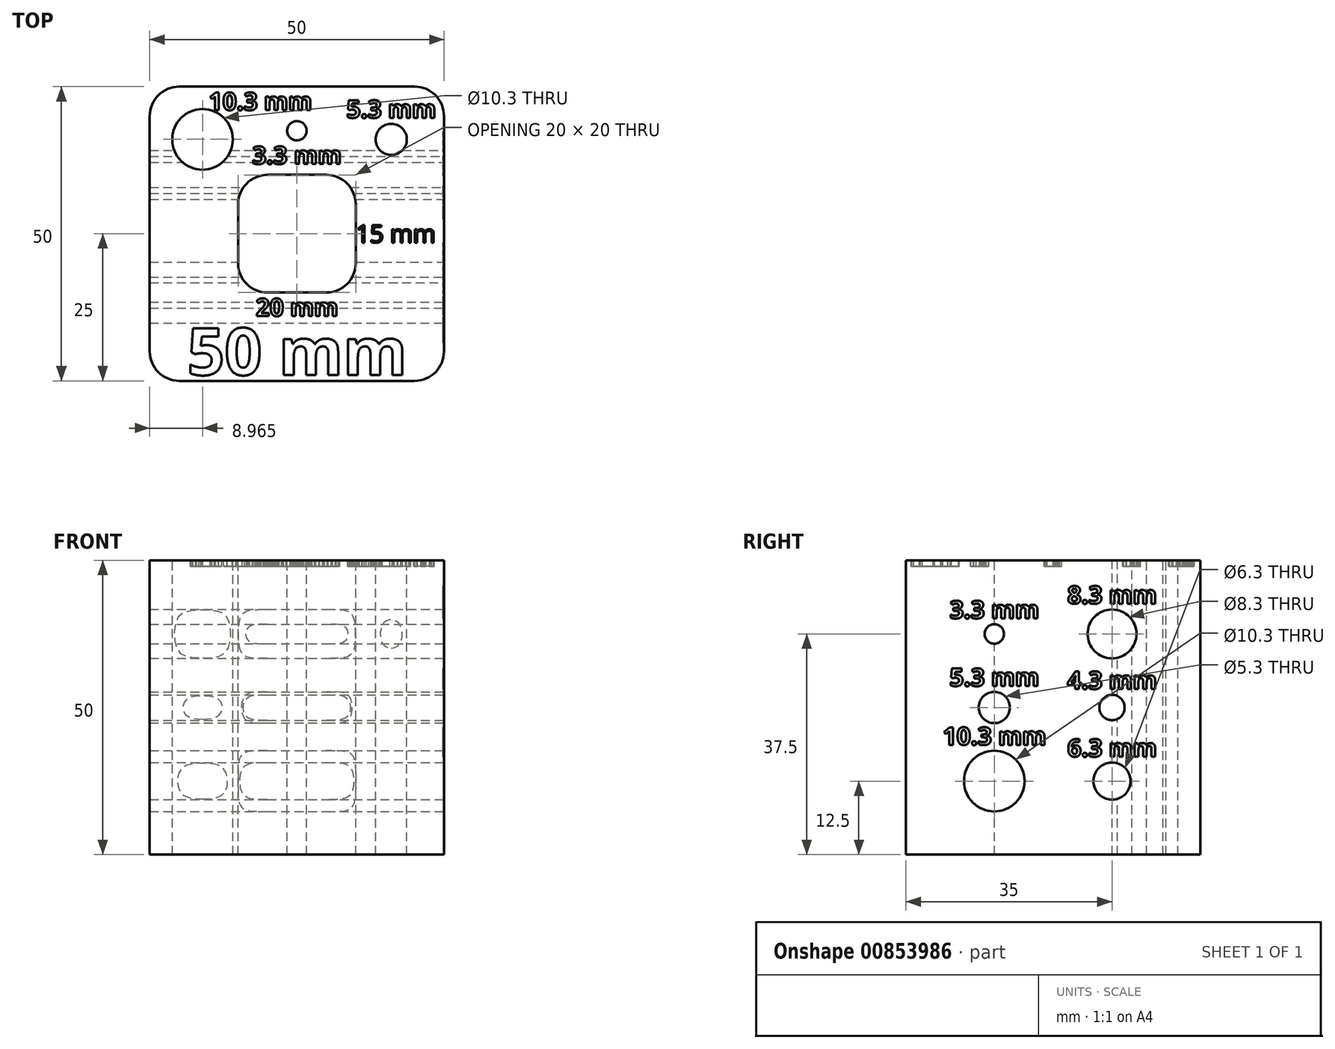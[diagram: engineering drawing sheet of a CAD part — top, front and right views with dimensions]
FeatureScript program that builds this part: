
annotation { "Feature Type Name" : "Feature", "Feature Type Description" : "" }
export const myFeature = defineFeature(function(context is Context, id is Id, definition is map)
    precondition{}
    {
        {
            var Q0;
            Q0=qCreatedBy(makeId("Top.planeOp"),FACE);
            var sketch = newSketch(context, id + "F0", { "sketchPlane" : qUnion([Q0])});
            skLineSegment(sketch, "E0.bottom", {"start": v(-25, 25) * mm, "end": v(25, 25) * mm});
            skLineSegment(sketch, "E0.top", {"start": v(-25, -25) * mm, "end": v(25, -25) * mm});
            skLineSegment(sketch, "E0.left", {"start": v(-25, 25) * mm, "end": v(-25, -25) * mm});
            skLineSegment(sketch, "E0.right", {"start": v(25, 25) * mm, "end": v(25, -25) * mm});
            skLineSegment(sketch, "E1", {"start": v(0, 25) * mm, "end": v(0, -25) * mm, "construction": true});
            skSolve(sketch);
        }
        {
            var Q0;
            Q0=makeQuery(id+"F0.imprint","IMPRINT",FACE,{"disambiguationData":[TD([[makeQuery(id+"F0.imprint","IMPRINT",EDGE,{"derivedFrom":sQuery(id+"F0.wireOp",EDGE,"E0.bottom")}),-1.0]])]});
            extrude(context, id + "F1", {"entities" : qUnion([Q0]), "depth" : 50 * mm, "offsetDistance" : 25 * mm});
        }
        {
            var Q0;
            Q0=makeQuery(id+"F1.opExtrude","CAP_FACE",FACE,{"disambiguationData":[OSD([sQuery(id+"F0.wireOp",EDGE,"E0.bottom"),sQuery(id+"F0.wireOp",EDGE,"E0.top"),sQuery(id+"F0.wireOp",EDGE,"E0.left"),sQuery(id+"F0.wireOp",EDGE,"E0.right")])],"isStart":false});
            var sketch = newSketch(context, id + "F2", { "sketchPlane" : qUnion([Q0])});
            skLineSegment(sketch, "E2.bottom", {"start": v(-10, 10) * mm, "end": v(10, 10) * mm});
            skLineSegment(sketch, "E2.top", {"start": v(-10, -10) * mm, "end": v(10, -10) * mm});
            skLineSegment(sketch, "E2.left", {"start": v(-10, 10) * mm, "end": v(-10, -10) * mm});
            skLineSegment(sketch, "E2.right", {"start": v(10, 10) * mm, "end": v(10, -10) * mm});
            skLineSegment(sketch, "E3", {"start": v(0, 10) * mm, "end": v(0, -10) * mm, "construction": true});
            skSolve(sketch);
        }
        {
            var Q0;
            Q0=makeQuery(id+"F2.imprint","IMPRINT",FACE,{"disambiguationData":[TD([[makeQuery(id+"F2.imprint","IMPRINT",EDGE,{"derivedFrom":sQuery(id+"F2.wireOp",EDGE,"E2.bottom")}),-1.0]])]});
            extrude(context, id + "F3", {"entities" : qUnion([Q0]), "operationType" : NewBodyOperationType.REMOVE, "endBound" : BoundingType.THROUGH_ALL, "oppositeDirection" : true, "depth" : 25 * mm, "offsetDistance" : 25 * mm});
        }
        {
            var Q0;
            Q0=makeQuery(id+"F1.opExtrude","SWEPT_EDGE",EDGE,{"disambiguationData":[OSD([sQuery(id+"F0.wireOp",EDGE,"E0.bottom"),sQuery(id+"F0.wireOp",EDGE,"E0.left")])]});
            var Q1;
            Q1=makeQuery(id+"F1.opExtrude","SWEPT_EDGE",EDGE,{"disambiguationData":[OSD([sQuery(id+"F0.wireOp",EDGE,"E0.bottom"),sQuery(id+"F0.wireOp",EDGE,"E0.right")])]});
            var Q2;
            Q2=makeQuery(id+"F1.opExtrude","SWEPT_EDGE",EDGE,{"disambiguationData":[OSD([sQuery(id+"F0.wireOp",EDGE,"E0.top"),sQuery(id+"F0.wireOp",EDGE,"E0.right")])]});
            var Q3;
            Q3=makeQuery(id+"F1.opExtrude","SWEPT_EDGE",EDGE,{"disambiguationData":[OSD([sQuery(id+"F0.wireOp",EDGE,"E0.top"),sQuery(id+"F0.wireOp",EDGE,"E0.left")])]});
            fillet(context, id + "F4", {"entities" : qUnion([Q0, Q1, Q2, Q3]), "radius" : 5 * mm, "tangentPropagation" : true, "allowEdgeOverflow" : false});
        }
        {
            var Q0;
            Q0=makeQuery(id+"F3.boolean.opBoolean","COPY",EDGE,{"derivedFrom":makeQuery(id+"F3.opExtrude","SWEPT_EDGE",EDGE,{"disambiguationData":[OSD([sQuery(id+"F2.wireOp",EDGE,"E2.bottom"),sQuery(id+"F2.wireOp",EDGE,"E2.right")])]})});
            var Q1;
            Q1=makeQuery(id+"F3.boolean.opBoolean","COPY",EDGE,{"derivedFrom":makeQuery(id+"F3.opExtrude","SWEPT_EDGE",EDGE,{"disambiguationData":[OSD([sQuery(id+"F2.wireOp",EDGE,"E2.bottom"),sQuery(id+"F2.wireOp",EDGE,"E2.left")])]})});
            var Q2;
            Q2=makeQuery(id+"F3.boolean.opBoolean","COPY",EDGE,{"derivedFrom":makeQuery(id+"F3.opExtrude","SWEPT_EDGE",EDGE,{"disambiguationData":[OSD([sQuery(id+"F2.wireOp",EDGE,"E2.top"),sQuery(id+"F2.wireOp",EDGE,"E2.right")])]})});
            var Q3;
            Q3=makeQuery(id+"F3.boolean.opBoolean","COPY",EDGE,{"derivedFrom":makeQuery(id+"F3.opExtrude","SWEPT_EDGE",EDGE,{"disambiguationData":[OSD([sQuery(id+"F2.wireOp",EDGE,"E2.top"),sQuery(id+"F2.wireOp",EDGE,"E2.left")])]})});
            fillet(context, id + "F5", {"entities" : qUnion([Q0, Q1, Q2, Q3]), "radius" : 5 * mm, "tangentPropagation" : true, "allowEdgeOverflow" : false});
        }
        {
            var Q0;
            Q0=makeQuery(id+"F1.opExtrude","CAP_FACE",FACE,{"disambiguationData":[OSD([sQuery(id+"F0.wireOp",EDGE,"E0.bottom"),sQuery(id+"F0.wireOp",EDGE,"E0.top"),sQuery(id+"F0.wireOp",EDGE,"E0.left"),sQuery(id+"F0.wireOp",EDGE,"E0.right")])],"isStart":false});
            var sketch = newSketch(context, id + "F6", { "sketchPlane" : qUnion([Q0])});
            skCircle(sketch, "E4", {"center": v(-16.04, 16.04) * mm, "radius": 5.15 * mm});
            skLineSegment(sketch, "E5", {"start": v(-23.54, 23.54) * mm, "end": v(-8.54, 8.54) * mm, "construction": true});
            skCircle(sketch, "E6", {"center": v(16.04, 16.04) * mm, "radius": 2.65 * mm});
            skLineSegment(sketch, "E7", {"start": v(8.54, 8.54) * mm, "end": v(23.54, 23.54) * mm, "construction": true});
            skCircle(sketch, "E8", {"center": v(0, 17.5) * mm, "radius": 1.65 * mm});
            skLineSegment(sketch, "E9", {"start": v(0, 25) * mm, "end": v(0, 10) * mm, "construction": true});
            skSolve(sketch);
        }
        {
            var Q0;
            Q0=makeQuery(id+"F6.imprint","IMPRINT",FACE,{"disambiguationData":[TD([[makeQuery(id+"F6.imprint","IMPRINT",EDGE,{"derivedFrom":sQuery(id+"F6.wireOp",EDGE,"E4")}),1.0]])]});
            var Q1;
            Q1=makeQuery(id+"F6.imprint","IMPRINT",FACE,{"disambiguationData":[TD([[makeQuery(id+"F6.imprint","IMPRINT",EDGE,{"derivedFrom":sQuery(id+"F6.wireOp",EDGE,"E8")}),1.0]])]});
            var Q2;
            Q2=makeQuery(id+"F6.imprint","IMPRINT",FACE,{"disambiguationData":[TD([[makeQuery(id+"F6.imprint","IMPRINT",EDGE,{"derivedFrom":sQuery(id+"F6.wireOp",EDGE,"E6")}),1.0]])]});
            extrude(context, id + "F7", {"entities" : qUnion([Q0, Q1, Q2]), "operationType" : NewBodyOperationType.REMOVE, "endBound" : BoundingType.THROUGH_ALL, "oppositeDirection" : true, "depth" : 25 * mm, "offsetDistance" : 25 * mm});
        }
        {
            var Q0;
            Q0=makeQuery(id+"F1.opExtrude","SWEPT_FACE",FACE,{"disambiguationData":[OSD([sQuery(id+"F0.wireOp",EDGE,"E0.right")])]});
            var sketch = newSketch(context, id + "F8", { "sketchPlane" : qUnion([Q0])});
            skCircle(sketch, "E10", {"center": v(-10, 37.5) * mm, "radius": 1.65 * mm});
            skCircle(sketch, "E11", {"center": v(10, 25) * mm, "radius": 2.15 * mm});
            skCircle(sketch, "E12", {"center": v(-10, 25) * mm, "radius": 2.65 * mm});
            skCircle(sketch, "E13", {"center": v(10, 12.5) * mm, "radius": 3.15 * mm});
            skCircle(sketch, "E14", {"center": v(10, 37.5) * mm, "radius": 4.15 * mm});
            skCircle(sketch, "E15", {"center": v(-10, 12.5) * mm, "radius": 5.15 * mm});
            skLineSegment(sketch, "E16", {"start": v(0, 50) * mm, "end": v(0, 0) * mm, "construction": true});
            skLineSegment(sketch, "E17", {"start": v(0, 25) * mm, "end": v(-20, 25) * mm, "construction": true});
            skLineSegment(sketch, "E18", {"start": v(-10, 25) * mm, "end": v(-10, 50) * mm, "construction": true});
            skLineSegment(sketch, "E19", {"start": v(-10, 25) * mm, "end": v(-10, 0) * mm, "construction": true});
            skLineSegment(sketch, "E20", {"start": v(0, 25) * mm, "end": v(20, 25) * mm, "construction": true});
            skLineSegment(sketch, "E21", {"start": v(10, 25) * mm, "end": v(10, 50) * mm, "construction": true});
            skLineSegment(sketch, "E22", {"start": v(10, 25) * mm, "end": v(10, 0) * mm, "construction": true});
            skSolve(sketch);
        }
        {
            var Q0;
            Q0=makeQuery(id+"F8.imprint","IMPRINT",FACE,{"disambiguationData":[TD([[makeQuery(id+"F8.imprint","IMPRINT",EDGE,{"derivedFrom":sQuery(id+"F8.wireOp",EDGE,"E10")}),1.0]])]});
            var Q1;
            Q1=makeQuery(id+"F8.imprint","IMPRINT",FACE,{"disambiguationData":[TD([[makeQuery(id+"F8.imprint","IMPRINT",EDGE,{"derivedFrom":sQuery(id+"F8.wireOp",EDGE,"E12")}),1.0]])]});
            var Q2;
            Q2=makeQuery(id+"F8.imprint","IMPRINT",FACE,{"disambiguationData":[TD([[makeQuery(id+"F8.imprint","IMPRINT",EDGE,{"derivedFrom":sQuery(id+"F8.wireOp",EDGE,"E15")}),1.0]])]});
            var Q3;
            Q3=makeQuery(id+"F8.imprint","IMPRINT",FACE,{"disambiguationData":[TD([[makeQuery(id+"F8.imprint","IMPRINT",EDGE,{"derivedFrom":sQuery(id+"F8.wireOp",EDGE,"E14")}),1.0]])]});
            var Q4;
            Q4=makeQuery(id+"F8.imprint","IMPRINT",FACE,{"disambiguationData":[TD([[makeQuery(id+"F8.imprint","IMPRINT",EDGE,{"derivedFrom":sQuery(id+"F8.wireOp",EDGE,"E11")}),1.0]])]});
            var Q5;
            Q5=makeQuery(id+"F8.imprint","IMPRINT",FACE,{"disambiguationData":[TD([[makeQuery(id+"F8.imprint","IMPRINT",EDGE,{"derivedFrom":sQuery(id+"F8.wireOp",EDGE,"E13")}),1.0]])]});
            extrude(context, id + "F9", {"entities" : qUnion([Q0, Q1, Q2, Q3, Q4, Q5]), "operationType" : NewBodyOperationType.REMOVE, "endBound" : BoundingType.THROUGH_ALL, "oppositeDirection" : true, "depth" : 25 * mm, "offsetDistance" : 25 * mm});
        }
        {
            var Q0;
            Q0=makeQuery(id+"F1.opExtrude","SWEPT_FACE",FACE,{"disambiguationData":[OSD([sQuery(id+"F0.wireOp",EDGE,"E0.right")])]});
            var sketch = newSketch(context, id + "F10", { "sketchPlane" : qUnion([Q0])});
            skText(sketch, "E23", { "text": "5.3 mm", "fontName": "OpenSans-Bold.ttf"});
            skLineSegment(sketch, "E24", {"start": v(-10, 37.5) * mm, "end": v(-10, 0) * mm, "construction": true});
            skLineSegment(sketch, "E25", {"start": v(-10, 37.5) * mm, "end": v(-10, 50) * mm, "construction": true});
            skText(sketch, "E26", { "text": "10.3 mm", "fontName": "OpenSans-Bold.ttf"});
            skText(sketch, "E27", { "text": "3.3 mm", "fontName": "OpenSans-Bold.ttf"});
            skText(sketch, "E28", { "text": "8.3 mm", "fontName": "OpenSans-Bold.ttf"});
            skLineSegment(sketch, "E29", {"start": v(10, 37.5) * mm, "end": v(10, 50) * mm, "construction": true});
            skLineSegment(sketch, "E30", {"start": v(10, 37.5) * mm, "end": v(10, 0) * mm, "construction": true});
            skText(sketch, "E31", { "text": "4.3 mm", "fontName": "OpenSans-Bold.ttf"});
            skText(sketch, "E32", { "text": "6.3 mm", "fontName": "OpenSans-Bold.ttf"});
            const initialGuessF10  = {"E23": [-0.01758, 0.02865, 1, 0, 0.003], "E26": [-0.01877, 0.01865, 1, 0, 0.003], "E27": [-0.01758, 0.04015, 1, 0, 0.003], "E28": [0.00242, 0.04265, 1, 0, 0.003], "E31": [0.00242, 0.02815, 1, 0, 0.003], "E32": [0.00242, 0.01665, 1, 0, 0.003]};
            skSetInitialGuess(sketch, initialGuessF10);
            skSolve(sketch);
        }
        {
            var Q0;
            Q0 = qSketchRegion(id + "F10", true);
            extrude(context, id + "F11", {"entities" : qUnion([Q0]), "operationType" : NewBodyOperationType.REMOVE, "oppositeDirection" : true, "depth" : 0.2 * mm, "offsetDistance" : 25 * mm});
        }
        {
            var Q0;
            Q0=makeQuery(id+"F1.opExtrude","CAP_FACE",FACE,{"disambiguationData":[OSD([sQuery(id+"F0.wireOp",EDGE,"E0.bottom"),sQuery(id+"F0.wireOp",EDGE,"E0.top"),sQuery(id+"F0.wireOp",EDGE,"E0.left"),sQuery(id+"F0.wireOp",EDGE,"E0.right")])],"isStart":false});
            var sketch = newSketch(context, id + "F12", { "sketchPlane" : qUnion([Q0])});
            skText(sketch, "E33", { "text": "50 mm", "fontName": "OpenSans-Bold.ttf"});
            skLineSegment(sketch, "E34", {"start": v(0, -10) * mm, "end": v(0, -25) * mm, "construction": true});
            skText(sketch, "E35", { "text": "15 mm", "fontName": "OpenSans-Regular.ttf"});
            skText(sketch, "E36", { "text": "3.3 mm", "fontName": "OpenSans-Bold.ttf"});
            skText(sketch, "E37", { "text": "10.3 mm", "fontName": "OpenSans-Bold.ttf"});
            skText(sketch, "E38", { "text": "5.3 mm", "fontName": "OpenSans-Bold.ttf"});
            skLineSegment(sketch, "E39", {"start": v(16.04, 16.04) * mm, "end": v(16.04, 25) * mm, "construction": true});
            skText(sketch, "E40", { "text": "20 mm", "fontName": "OpenSans-Bold.ttf"});
            const initialGuessF12  = {"E33": [-0.01864, -0.024, 1, 0, 0.008], "E35": [0.01, -0.0015, 1, 0, 0.003], "E36": [-0.00758, 0.01185, 1, 0, 0.003], "E37": [-0.015, 0.021, 1, 0, 0.003], "E38": [0.00845, 0.01969, 1, 0, 0.003], "E40": [-0.007, -0.014, 1, 0, 0.003]};
            skSetInitialGuess(sketch, initialGuessF12);
            skSolve(sketch);
        }
        {
            var Q0;
            Q0 = qSketchRegion(id + "F12", true);
            extrude(context, id + "F13", {"entities" : qUnion([Q0]), "operationType" : NewBodyOperationType.REMOVE, "oppositeDirection" : true, "depth" : 1 * mm, "offsetDistance" : 25 * mm});
        }
    });
